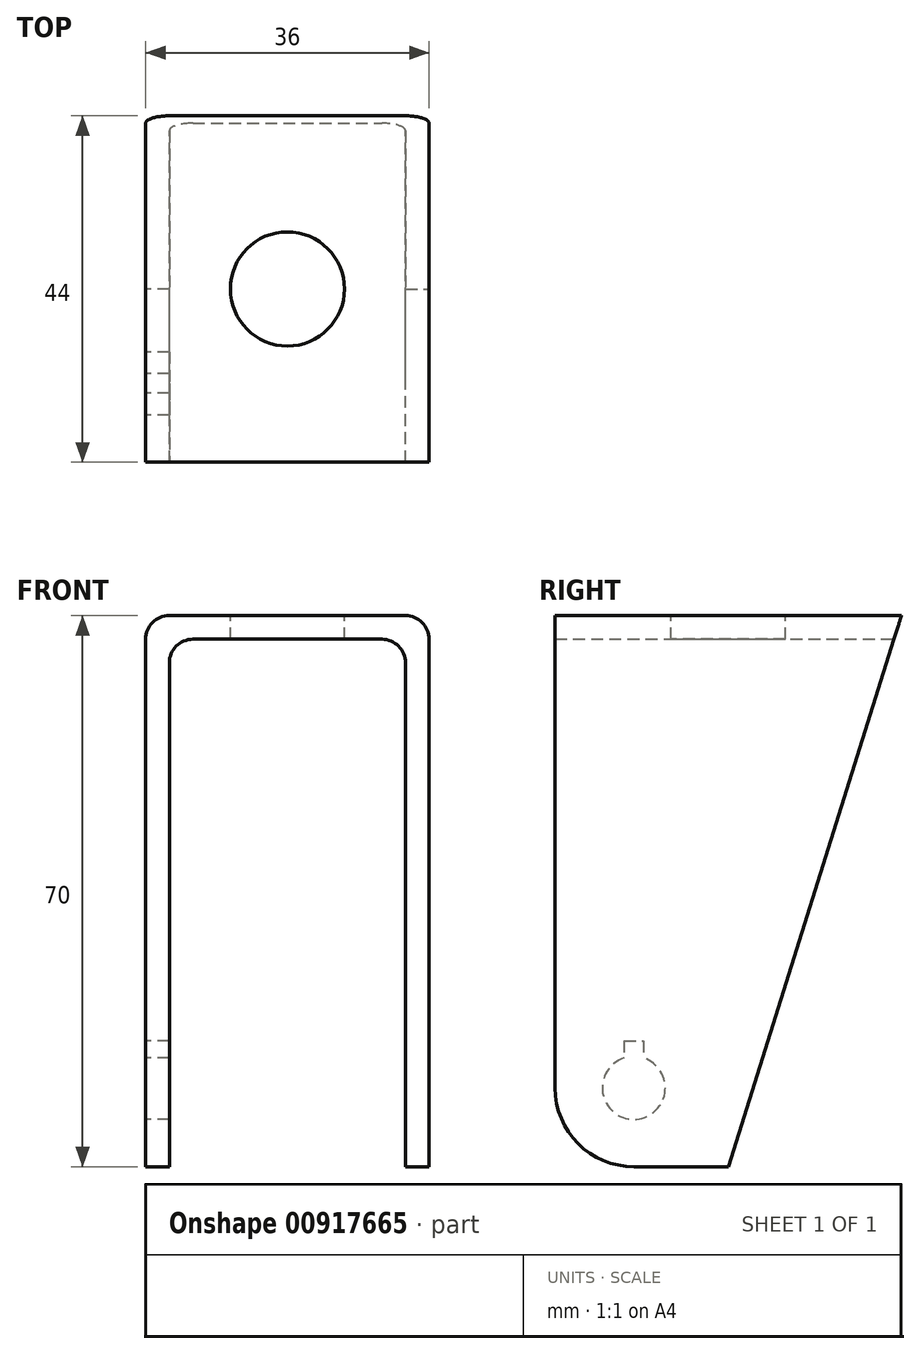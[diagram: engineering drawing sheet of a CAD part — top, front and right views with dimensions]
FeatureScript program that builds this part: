
annotation { "Feature Type Name" : "Feature", "Feature Type Description" : "" }
export const myFeature = defineFeature(function(context is Context, id is Id, definition is map)
    precondition{}
    {
        {
            var Q0;
            Q0=qCreatedBy(makeId("Front.planeOp"),FACE);
            var sketch = newSketch(context, id + "F0", { "sketchPlane" : qUnion([Q0])});
            skLineSegment(sketch, "E0", {"start": v(0, 0) * mm, "end": v(0, 70) * mm});
            skLineSegment(sketch, "E1", {"start": v(0, 70) * mm, "end": v(36, 70) * mm});
            skLineSegment(sketch, "E2", {"start": v(36, 70) * mm, "end": v(36, 0) * mm});
            skLineSegment(sketch, "E3", {"start": v(0, 0) * mm, "end": v(3, 0) * mm});
            skLineSegment(sketch, "E4", {"start": v(3, 0) * mm, "end": v(3, 67) * mm});
            skLineSegment(sketch, "E5", {"start": v(3, 67) * mm, "end": v(33, 67) * mm});
            skLineSegment(sketch, "E6", {"start": v(33, 67) * mm, "end": v(33, 0) * mm});
            skLineSegment(sketch, "E7", {"start": v(33, 0) * mm, "end": v(36, 0) * mm});
            skSolve(sketch);
        }
        {
            var Q0;
            Q0 = qSketchRegion(id + "F0", true);
            extrude(context, id + "F1", {"entities" : qUnion([Q0]), "depth" : 44 * mm, "offsetDistance" : 25 * mm});
        }
        {
            var Q0;
            Q0=makeQuery(id+"F1.opExtrude","SWEPT_FACE",FACE,{"disambiguationData":[OSD([sQuery(id+"F0.wireOp",EDGE,"E2")])]});
            var sketch = newSketch(context, id + "F2", { "sketchPlane" : qUnion([Q0])});
            skCircle(sketch, "E8", {"center": v(-34, 10) * mm, "radius": 4 * mm});
            skLineSegment(sketch, "E9", {"start": v(0, 70) * mm, "end": v(-22, 0) * mm});
            skSolve(sketch);
        }
        {
            var Q0;
            Q0=makeQuery(id+"F2.imprint","IMPRINT",FACE,{"disambiguationData":[TD([[makeQuery(id+"F2.imprint","IMPRINT",EDGE,{"derivedFrom":sQuery(id+"F2.wireOp",EDGE,"E8")}),1.0]])]});
            var sketch = newSketch(context, id + "F3", { "sketchPlane" : qUnion([Q0])});
            skSolve(sketch);
        }
        {
            var Q0;
            {var subQ0=sQuery(id+"F2.wireOp",EDGE,"E9");Q0=makeQuery(id+"F2.imprint","IMPRINT",FACE,{"disambiguationData":[TD([[makeQuery(id+"F2.imprint","IMPRINT",EDGE,{"derivedFrom":subQ0}),1.0]])]});}
            var Q1;
            Q1=makeQuery(id+"F3.imprint","IMPRINT",FACE,{"disambiguationData":[TD([[makeQuery(id+"F3.imprint","IMPRINT",EDGE,{"derivedFrom":makeQuery(id+"F2.imprint","IMPRINT",EDGE,{"derivedFrom":sQuery(id+"F2.wireOp",EDGE,"E8")})}),1.0]])]});
            extrude(context, id + "F4", {"entities" : qUnion([Q0, Q1]), "operationType" : NewBodyOperationType.REMOVE, "oppositeDirection" : true, "depth" : 25 * mm, "offsetDistance" : 25 * mm});
        }
        {
            var Q0;
            Q0=makeQuery(id+"F1.opExtrude","SWEPT_FACE",FACE,{"disambiguationData":[OSD([sQuery(id+"F0.wireOp",EDGE,"E0")])]});
            var sketch = newSketch(context, id + "F5", { "sketchPlane" : qUnion([Q0])});
            skLineSegment(sketch, "E10", {"start": v(0, 70) * mm, "end": v(22, 0) * mm});
            skArc(sketch, "E11", {"start": v(32.75, 13.8) * mm, "mid": v(34, 6) * mm, "end": v(35.25, 13.8) * mm});
            skLineSegment(sketch, "E12", {"start": v(34, 16) * mm, "end": v(32.75, 16) * mm});
            skLineSegment(sketch, "E13", {"start": v(32.75, 16) * mm, "end": v(32.75, 13.8) * mm});
            skLineSegment(sketch, "E14", {"start": v(34, 16) * mm, "end": v(35.25, 16) * mm});
            skLineSegment(sketch, "E15", {"start": v(35.25, 16) * mm, "end": v(35.25, 13.8) * mm});
            skSolve(sketch);
        }
        {
            var Q0;
            {var subQ0=sQuery(id+"F5.wireOp",EDGE,"E10");Q0=makeQuery(id+"F5.imprint","IMPRINT",FACE,{"disambiguationData":[TD([[makeQuery(id+"F5.imprint","IMPRINT",EDGE,{"derivedFrom":subQ0}),-1.0]])]});}
            var Q1;
            Q1=makeQuery(id+"F5.imprint","IMPRINT",FACE,{"disambiguationData":[TD([[makeQuery(id+"F5.imprint","IMPRINT",EDGE,{"derivedFrom":sQuery(id+"F5.wireOp",EDGE,"E11")}),1.0]])]});
            extrude(context, id + "F6", {"entities" : qUnion([Q0, Q1]), "operationType" : NewBodyOperationType.REMOVE, "oppositeDirection" : true, "depth" : 25 * mm, "offsetDistance" : 25 * mm});
        }
        {
            var Q0;
            Q0=makeQuery(id+"F1.opExtrude","SWEPT_EDGE",EDGE,{"disambiguationData":[OSD([sQuery(id+"F0.wireOp",EDGE,"E5"),sQuery(id+"F0.wireOp",EDGE,"E6")])]});
            var Q1;
            Q1=makeQuery(id+"F1.opExtrude","SWEPT_EDGE",EDGE,{"disambiguationData":[OSD([sQuery(id+"F0.wireOp",EDGE,"E4"),sQuery(id+"F0.wireOp",EDGE,"E5")])]});
            var Q2;
            Q2=makeQuery(id+"F1.opExtrude","SWEPT_EDGE",EDGE,{"disambiguationData":[OSD([sQuery(id+"F0.wireOp",EDGE,"E1"),sQuery(id+"F0.wireOp",EDGE,"E2")])]});
            var Q3;
            Q3=makeQuery(id+"F1.opExtrude","SWEPT_EDGE",EDGE,{"disambiguationData":[OSD([sQuery(id+"F0.wireOp",EDGE,"E0"),sQuery(id+"F0.wireOp",EDGE,"E1")])]});
            fillet(context, id + "F7", {"entities" : qUnion([Q0, Q1, Q2, Q3]), "radius" : 3 * mm, "tangentPropagation" : true, "allowEdgeOverflow" : false});
        }
        {
            var Q0;
            Q0=makeQuery(id+"F1.opExtrude","CAP_EDGE",EDGE,{"disambiguationData":[OSD([sQuery(id+"F0.wireOp",EDGE,"E3")])],"isStart":false});
            var Q1;
            Q1=makeQuery(id+"F1.opExtrude","CAP_EDGE",EDGE,{"disambiguationData":[OSD([sQuery(id+"F0.wireOp",EDGE,"E7")])],"isStart":false});
            var Q2;
            Q2=makeQuery(id+"F6.boolean.opBoolean","COPY",EDGE,{"derivedFrom":makeQuery(id+"F6.opExtrude","SWEPT_EDGE",EDGE,{"disambiguationData":[OSD([sQuery(id+"F0.wireOp",EDGE,"E0"),sQuery(id+"F0.wireOp",EDGE,"E3"),sQuery(id+"F5.wireOp",EDGE,"E10")])]})});
            var Q3;
            Q3=makeQuery(id+"F4.boolean.opBoolean","COPY",EDGE,{"derivedFrom":makeQuery(id+"F4.opExtrude","SWEPT_EDGE",EDGE,{"disambiguationData":[OSD([sQuery(id+"F0.wireOp",EDGE,"E2"),sQuery(id+"F0.wireOp",EDGE,"E7"),sQuery(id+"F2.wireOp",EDGE,"E9")])]})});
            fillet(context, id + "F8", {"entities" : qUnion([Q0, Q1, Q2, Q3]), "radius" : 10 * mm, "tangentPropagation" : true, "allowEdgeOverflow" : false});
        }
        {
            var Q0;
            Q0=makeQuery(id+"F1.opExtrude","SWEPT_FACE",FACE,{"disambiguationData":[OSD([sQuery(id+"F0.wireOp",EDGE,"E1")])]});
            var sketch = newSketch(context, id + "F9", { "sketchPlane" : qUnion([Q0])});
            skCircle(sketch, "E16", {"center": v(18, -22) * mm, "radius": 7.25 * mm});
            skSolve(sketch);
        }
        {
            var Q0;
            Q0 = qSketchRegion(id + "F9", true);
            extrude(context, id + "F10", {"entities" : qUnion([Q0]), "operationType" : NewBodyOperationType.REMOVE, "oppositeDirection" : true, "depth" : 25 * mm, "offsetDistance" : 25 * mm});
        }
    });
